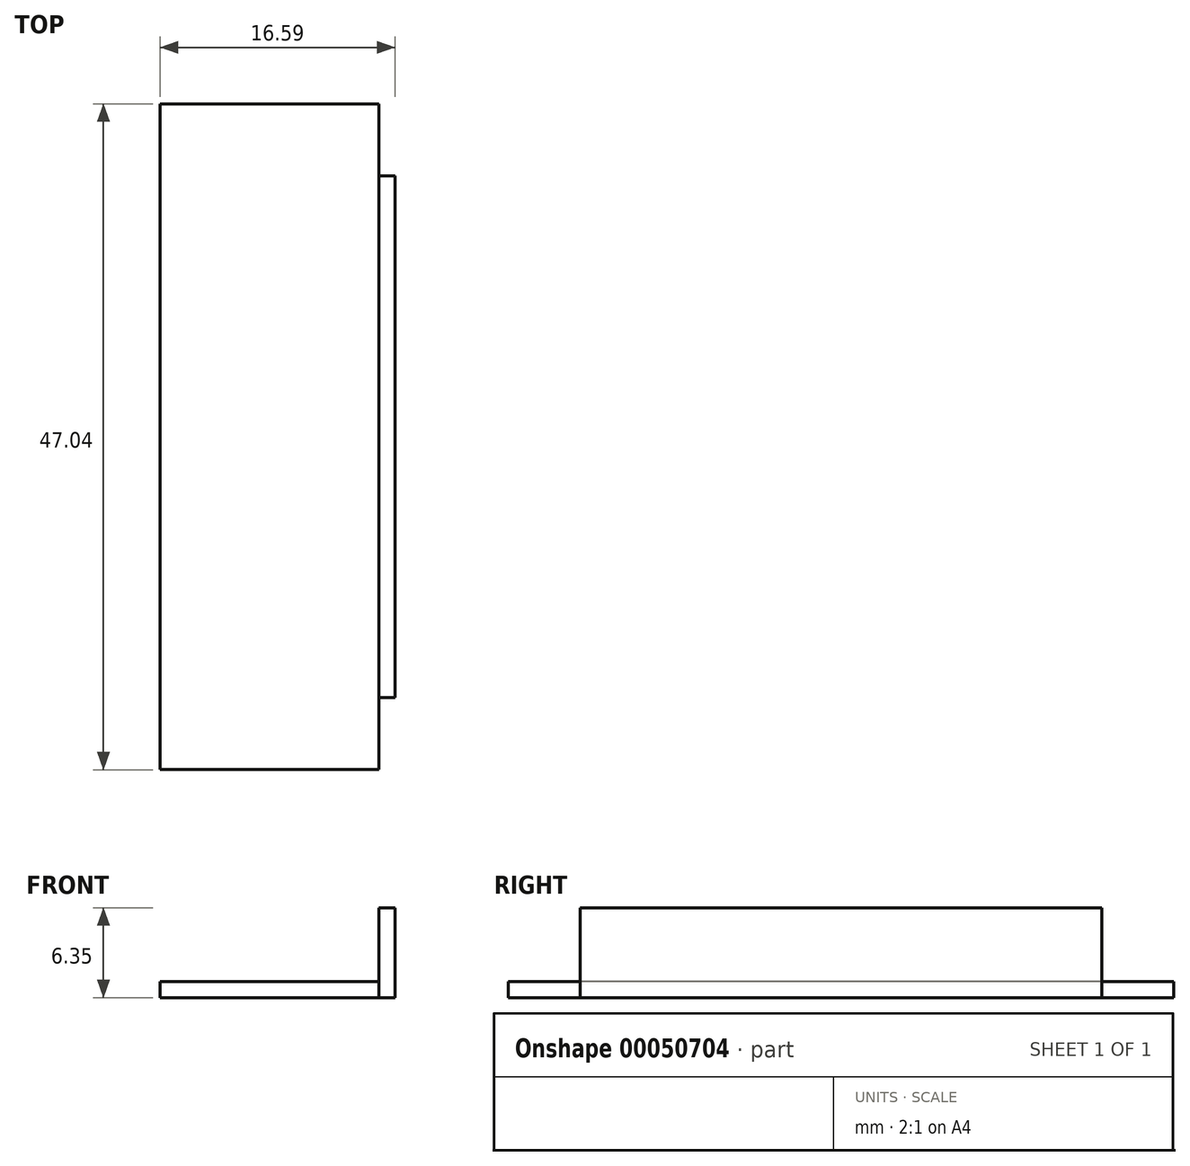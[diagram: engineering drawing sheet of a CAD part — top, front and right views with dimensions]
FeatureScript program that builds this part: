
annotation { "Feature Type Name" : "Feature", "Feature Type Description" : "" }
export const myFeature = defineFeature(function(context is Context, id is Id, definition is map)
    precondition{}
    {
        {
            var Q0;
            Q0=qCreatedBy(makeId("Top.planeOp"),FACE);
            var sketch = newSketch(context, id + "F0", { "sketchPlane" : qUnion([Q0])});
            skLineSegment(sketch, "E0", {"start": v(-5.22, 31.73) * mm, "end": v(10.25, 31.73) * mm});
            skLineSegment(sketch, "E1", {"start": v(10.25, 31.73) * mm, "end": v(10.25, 26.65) * mm});
            skLineSegment(sketch, "E2", {"start": v(10.25, 26.65) * mm, "end": v(10.25, -10.23) * mm});
            skLineSegment(sketch, "E3", {"start": v(10.25, -10.23) * mm, "end": v(10.25, -15.3) * mm});
            skLineSegment(sketch, "E4", {"start": v(10.25, -15.3) * mm, "end": v(-5.22, -15.3) * mm});
            skLineSegment(sketch, "E5", {"start": v(-5.22, 31.73) * mm, "end": v(-5.22, -15.3) * mm});
            skSolve(sketch);
        }
        {
            var Q0;
            Q0 = qSketchRegion(id + "F0", true);
            extrude(context, id + "F1", {"entities" : qUnion([Q0]), "depth" : 1.12 * mm});
        }
        {
            var Q0;
            Q0=makeQuery(id+"F1.opExtrude","SWEPT_FACE",FACE,{"disambiguationData":[OSD([sQuery(id+"F0.wireOp",EDGE,"E1"),sQuery(id+"F0.wireOp",EDGE,"E2"),sQuery(id+"F0.wireOp",EDGE,"E3")])]});
            var sketch = newSketch(context, id + "F2", { "sketchPlane" : qUnion([Q0])});
            skLineSegment(sketch, "E6", {"start": v(-15.3, 0) * mm, "end": v(-10.23, 0) * mm});
            skLineSegment(sketch, "E7", {"start": v(-10.23, 0) * mm, "end": v(-10.23, 6.35) * mm});
            skLineSegment(sketch, "E8", {"start": v(31.73, 0) * mm, "end": v(26.65, 0) * mm});
            skLineSegment(sketch, "E9", {"start": v(26.65, 0) * mm, "end": v(26.65, 6.35) * mm});
            skLineSegment(sketch, "E10", {"start": v(-10.23, 6.35) * mm, "end": v(26.65, 6.35) * mm});
            skLineSegment(sketch, "E11", {"start": v(-10.23, 0) * mm, "end": v(26.65, 0) * mm});
            skSolve(sketch);
        }
        {
            var Q0;
            Q0 = qSketchRegion(id + "F2", true);
            extrude(context, id + "F3", {"entities" : qUnion([Q0]), "operationType" : NewBodyOperationType.ADD, "depth" : 1.12 * mm});
        }
    });
